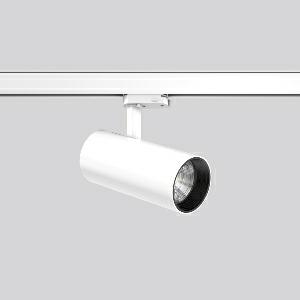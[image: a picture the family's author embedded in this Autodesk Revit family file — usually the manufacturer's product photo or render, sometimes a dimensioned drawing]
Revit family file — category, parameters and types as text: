
# Revit family: deecos_s_mini_742201_002_76_7ef9
name_source: partatom
category: Lighting Fixtures
units: mm (PartAtom-declared; Revit-internal decimal feet)

## family parameters
Cut with Voids When Loaded = No
Host = Face
Light Source = No
Part Type = Normal
Room Calculation Point = No
Round Connector Dimension = Use Diameter
Shared = No

## types (1)
- DEECOS S mini (1 x LED Modul 930, 2250 lm, 3000)
    Apparent Load = 20 VA
    Approval mark = CE
    CIE Flux Codes = 80 99 100 100 100
    Color Rendering = 90
    Color Temperature = 3000
    Default Elevation = 1800 mm
    Description = Series: DEECOS S mini
LED surface-mounted projector in modern design with no visible cooling ribs. Housing: die-cast aluminium, powder-coated. Rotation range: 356°. Swivel range: 90°. Black plastic ring and recessed LED to prevent glare from the side. Optical assembly with lens made of plastic (polycarbonate) for the best homogeneous light distribution - can be changed without tools. Best colour rendering index Ra>90. With adapter for RZB 3-circuit DALI tracks. Suitable for Track on ceiling, Wall track. High quality converter without flickering and stroboscopic effect. The following accessories can be mounted without use of tools: interchangeable lenses, decorative glasses, honeycomb louvre, clear and frosted diffusers, white interchangeable plastic ring. 
Colour: traffic white, matt (RAL 9016)
Diameter: 87 mm
Height: 214 mm
Lamp: LED
Socket: without socket
Colour temperature: 3000K
Colour rendering index (CRI): 92
System power: 20 W
Rated luminous flux: 2250 lm
Luminous efficiency: 113 lm/W
Control gear: Converter, dimmable, DALI
Protection class: I
Type of protection: IP 20
    Height = 214 mm
    Lamp = 1 x LED Modul 930
    Lamp Light Flux = 2250 lm
    Lamp count = 1
    Length = 87 mm
    Lifetime = 50000 h
    Luminous efficacy = 113 lm/W
    Manufacturer = RZB
    ModVariant = No
    Model = 742201.002.76
    Mounting Place = Ceiling
    Mounting Type = Rail mounted
    Number of Poles = 1
    OnlyDefault = Yes
    Power Factor = 1
    Product Name = DEECOS S mini
    Product group = Track mounted projectors
    ProductGroupID = 301
    Protection Class = Protection class I
    Protection Degree = IP 20
    RLX_Detail_Level = 1
    RLX_Emergency_Light_Flux = 0 lm
    RLX_Emergency_Type = 0
    RLX_Emergency_Type_DB = No
    RlxData = <blob elided: 35113 chars, md5=334eb44b>
    Socket = socket
    Standby Power = 0 W
    System Light Flux = 2250 lm
    System Power = 20 W
    Type Comments = Product without accessories
    Type Image = 741930.002.jpg
    URL = http://relux.com
    VarID = ---
    Voltage = 230 V
    Voltage Range = 220-240 V
    Weight = 0.00 kg
    Width = 0 mm  [stored 0 ft]

note: [stored X ft] marks values corroborated as IEEE doubles in the binary element streams (Revit-internal decimal feet)

## geometry (parser evidence)
native form markers: Blend x4, Sweep x12
no freeform markers — native parametric forms only
